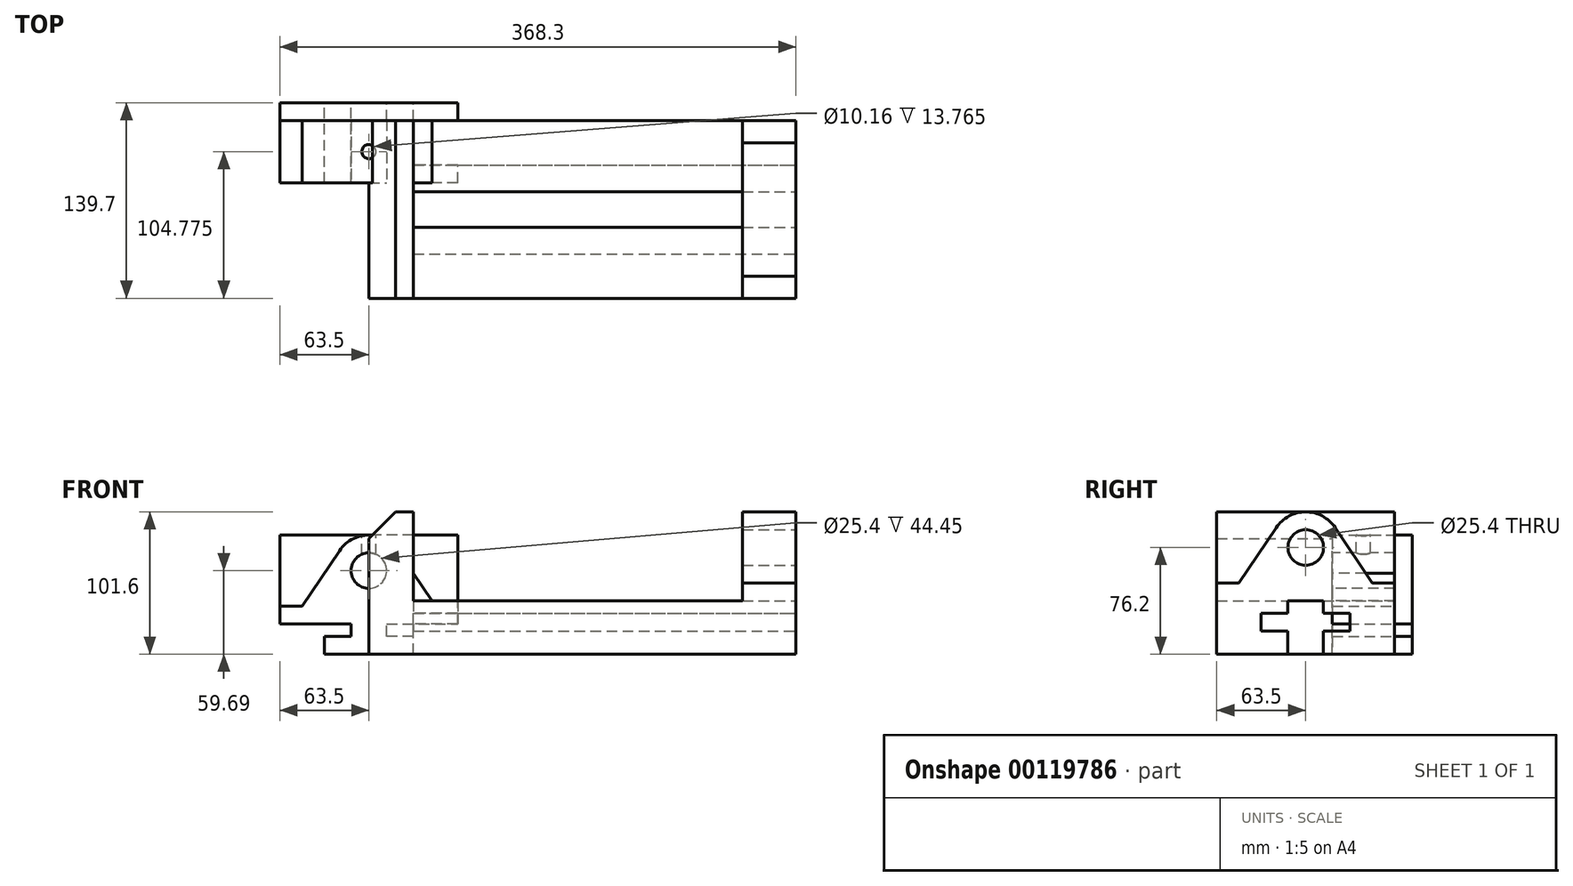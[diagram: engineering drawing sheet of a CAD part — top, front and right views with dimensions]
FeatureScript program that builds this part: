
annotation { "Feature Type Name" : "Feature", "Feature Type Description" : "" }
export const myFeature = defineFeature(function(context is Context, id is Id, definition is map)
    precondition{}
    {
        {
            var Q0;
            Q0=qCreatedBy(makeId("Front.planeOp"),FACE);
            var sketch = newSketch(context, id + "F0", { "sketchPlane" : qUnion([Q0])});
            skLineSegment(sketch, "E0", {"start": v(0, 0) * mm, "end": v(304.8, 0) * mm});
            skLineSegment(sketch, "E1", {"start": v(31.75, 38.1) * mm, "end": v(31.75, 101.6) * mm});
            skLineSegment(sketch, "E2", {"start": v(0, 101.6) * mm, "end": v(0, 0) * mm});
            skLineSegment(sketch, "E3", {"start": v(0, 101.6) * mm, "end": v(31.75, 101.6) * mm});
            skLineSegment(sketch, "E4", {"start": v(31.75, 38.1) * mm, "end": v(266.7, 38.1) * mm});
            skLineSegment(sketch, "E5", {"start": v(266.7, 38.1) * mm, "end": v(266.7, 101.6) * mm});
            skLineSegment(sketch, "E6", {"start": v(266.7, 101.6) * mm, "end": v(304.8, 101.6) * mm});
            skLineSegment(sketch, "E7", {"start": v(304.8, 101.6) * mm, "end": v(304.8, 0) * mm});
            skSolve(sketch);
        }
        {
            var Q0;
            Q0 = qSketchRegion(id + "F0", true);
            extrude(context, id + "F1", {"entities" : qUnion([Q0]), "depth" : 127 * mm});
        }
        {
            var Q0;
            Q0=makeQuery(id+"F1.opExtrude","SWEPT_EDGE",EDGE,{"disambiguationData":[OSD([sQuery(id+"F0.wireOp",EDGE,"E2"),sQuery(id+"F0.wireOp",EDGE,"E3")])]});
            chamfer(context, id + "F2", {"entities" : qUnion([Q0]), "chamferType" : ChamferType.TWO_OFFSETS, "width1" : 19.05 * mm, "oppositeDirection" : false, "width2" : 19.05 * mm, "tangentPropagation" : true});
        }
        {
            var Q0;
            Q0=makeQuery(id+"F1.opExtrude","SWEPT_FACE",FACE,{"disambiguationData":[OSD([sQuery(id+"F0.wireOp",EDGE,"E7")])]});
            var sketch = newSketch(context, id + "F3", { "sketchPlane" : qUnion([Q0])});
            skLineSegment(sketch, "E8", {"start": v(-127, 50.8) * mm, "end": v(-111.13, 50.8) * mm});
            skLineSegment(sketch, "E9", {"start": v(-111.13, 50.8) * mm, "end": v(-84.6, 90.35) * mm});
            skLineSegment(sketch, "E10", {"start": v(0, 50.8) * mm, "end": v(-15.87, 50.8) * mm});
            skLineSegment(sketch, "E11", {"start": v(-15.87, 50.8) * mm, "end": v(-42.4, 90.35) * mm});
            skArc(sketch, "E12", {"start": v(-42.4, 90.35) * mm, "mid": v(-63.5, 101.6) * mm, "end": v(-84.6, 90.35) * mm});
            skSolve(sketch);
        }
        {
            var Q0;
            Q0 = qSketchRegion(id + "F3", true);
            var Q1;
            {var subQ7=sQuery(id+"F3.wireOp",EDGE,"E8");Q1=makeQuery(id+"F3.imprint","IMPRINT",FACE,{"disambiguationData":[TD([[makeQuery(id+"F3.imprint","IMPRINT",EDGE,{"derivedFrom":subQ7}),1.0]])]});}
            var Q2;
            {var subQ7=sQuery(id+"F3.wireOp",EDGE,"E10");Q2=makeQuery(id+"F3.imprint","IMPRINT",FACE,{"disambiguationData":[TD([[makeQuery(id+"F3.imprint","IMPRINT",EDGE,{"derivedFrom":subQ7}),-1.0]])]});}
            extrude(context, id + "F4", {"entities" : qUnion([Q0, Q1, Q2]), "operationType" : NewBodyOperationType.REMOVE, "oppositeDirection" : true, "depth" : 50.8 * mm});
        }
        {
            var Q0;
            {var subQ6=sQuery(id+"F3.wireOp",EDGE,"E8");Q0=makeQuery(id+"F3.imprint","IMPRINT",FACE,{"disambiguationData":[TD([[makeQuery(id+"F3.imprint","IMPRINT",EDGE,{"derivedFrom":subQ6}),-1.0]])]});}
            var sketch = newSketch(context, id + "F5", { "sketchPlane" : qUnion([Q0])});
            skCircle(sketch, "E13", {"center": v(-63.5, 76.2) * mm, "radius": 12.7 * mm});
            skSolve(sketch);
        }
        {
            var Q0;
            Q0 = qSketchRegion(id + "F5", true);
            extrude(context, id + "F6", {"entities" : qUnion([Q0]), "operationType" : NewBodyOperationType.REMOVE, "oppositeDirection" : true, "depth" : 50.8 * mm});
        }
        {
            var Q0;
            {var subQ6=sQuery(id+"F3.wireOp",EDGE,"E8");Q0=makeQuery(id+"F3.imprint","IMPRINT",FACE,{"disambiguationData":[TD([[makeQuery(id+"F3.imprint","IMPRINT",EDGE,{"derivedFrom":subQ6}),-1.0]])]});}
            var sketch = newSketch(context, id + "F7", { "sketchPlane" : qUnion([Q0])});
            skLineSegment(sketch, "E14", {"start": v(-76.2, 0) * mm, "end": v(-76.2, 16.5) * mm});
            skLineSegment(sketch, "E15", {"start": v(-76.2, 16.5) * mm, "end": v(-95.25, 16.5) * mm});
            skLineSegment(sketch, "E16", {"start": v(-95.25, 16.5) * mm, "end": v(-95.25, 29.2) * mm});
            skLineSegment(sketch, "E17", {"start": v(-95.25, 29.2) * mm, "end": v(-76.2, 29.2) * mm});
            skLineSegment(sketch, "E18", {"start": v(-76.2, 29.2) * mm, "end": v(-76.2, 38.1) * mm});
            skLineSegment(sketch, "E19", {"start": v(-76.2, 38.1) * mm, "end": v(-50.8, 38.1) * mm});
            skLineSegment(sketch, "E20", {"start": v(-50.8, 38.1) * mm, "end": v(-50.8, 29.2) * mm});
            skLineSegment(sketch, "E21", {"start": v(-50.8, 29.2) * mm, "end": v(-31.75, 29.2) * mm});
            skLineSegment(sketch, "E22", {"start": v(-31.75, 29.2) * mm, "end": v(-31.75, 16.5) * mm});
            skLineSegment(sketch, "E23", {"start": v(-31.75, 16.5) * mm, "end": v(-50.8, 16.5) * mm});
            skLineSegment(sketch, "E24", {"start": v(-50.8, 16.5) * mm, "end": v(-50.8, 0) * mm});
            skLineSegment(sketch, "E25", {"start": v(-50.8, 0) * mm, "end": v(-76.2, 0) * mm});
            skSolve(sketch);
        }
        {
            var Q0;
            Q0 = qSketchRegion(id + "F7", true);
            var Q1;
            Q1=makeQuery(id+"F1.opExtrude","SWEPT_FACE",FACE,{"disambiguationData":[OSD([sQuery(id+"F0.wireOp",EDGE,"E1")])]});
            extrude(context, id + "F8", {"entities" : qUnion([Q0]), "operationType" : NewBodyOperationType.REMOVE, "endBound" : BoundingType.UP_TO_SURFACE, "oppositeDirection" : true, "endBoundEntityFace" : qUnion([Q1]), "depth" : 25.4 * mm});
        }
        {
            var Q0;
            Q0=qCreatedBy(makeId("Front.planeOp"),FACE);
            var sketch = newSketch(context, id + "F9", { "sketchPlane" : qUnion([Q0])});
            skLineSegment(sketch, "E26", {"start": v(0, 129.38) * mm, "end": v(0, -77.33) * mm, "construction": true});
            skLineSegment(sketch, "E27", {"start": v(-31.75, 0) * mm, "end": v(31.75, 0) * mm});
            skLineSegment(sketch, "E28", {"start": v(31.75, 0) * mm, "end": v(31.75, 12.7) * mm});
            skLineSegment(sketch, "E29", {"start": v(31.75, 12.7) * mm, "end": v(12.7, 12.7) * mm});
            skLineSegment(sketch, "E30", {"start": v(12.7, 12.7) * mm, "end": v(12.7, 21.6) * mm});
            skLineSegment(sketch, "E31", {"start": v(12.7, 21.59) * mm, "end": v(63.5, 21.59) * mm});
            skLineSegment(sketch, "E32", {"start": v(63.5, 21.59) * mm, "end": v(63.5, 34.3) * mm});
            skLineSegment(sketch, "E33", {"start": v(63.5, 34.3) * mm, "end": v(47.63, 34.3) * mm});
            skLineSegment(sketch, "E34", {"start": v(47.63, 34.29) * mm, "end": v(21.1, 73.84) * mm});
            skLineSegment(sketch, "E35", {"start": v(-31.75, 0) * mm, "end": v(-31.75, 12.7) * mm});
            skLineSegment(sketch, "E36", {"start": v(-31.75, 12.7) * mm, "end": v(-12.7, 12.7) * mm});
            skLineSegment(sketch, "E37", {"start": v(-12.7, 12.7) * mm, "end": v(-12.7, 21.59) * mm});
            skLineSegment(sketch, "E38", {"start": v(-12.7, 21.59) * mm, "end": v(-63.5, 21.59) * mm});
            skLineSegment(sketch, "E39", {"start": v(-63.5, 21.6) * mm, "end": v(-63.5, 34.3) * mm});
            skLineSegment(sketch, "E40", {"start": v(-63.5, 34.3) * mm, "end": v(-47.62, 34.3) * mm});
            skLineSegment(sketch, "E41", {"start": v(-47.62, 34.3) * mm, "end": v(-21.1, 73.84) * mm});
            skArc(sketch, "E42", {"start": v(21.1, 73.84) * mm, "mid": v(0, 85.1) * mm, "end": v(-21.1, 73.84) * mm});
            skSolve(sketch);
        }
        {
            var Q0;
            Q0 = qSketchRegion(id + "F9", true);
            extrude(context, id + "F10", {"entities" : qUnion([Q0]), "depth" : 44.45 * mm});
        }
        {
            var Q0;
            Q0=makeQuery(id+"F10.opExtrude","CAP_FACE",FACE,{"disambiguationData":[OSD([sQuery(id+"F9.wireOp",EDGE,"E27"),sQuery(id+"F9.wireOp",EDGE,"E28"),sQuery(id+"F9.wireOp",EDGE,"E29"),sQuery(id+"F9.wireOp",EDGE,"E30"),sQuery(id+"F9.wireOp",EDGE,"E31"),sQuery(id+"F9.wireOp",EDGE,"E32"),sQuery(id+"F9.wireOp",EDGE,"E33"),sQuery(id+"F9.wireOp",EDGE,"E34"),sQuery(id+"F9.wireOp",EDGE,"E35"),sQuery(id+"F9.wireOp",EDGE,"E36"),sQuery(id+"F9.wireOp",EDGE,"E37"),sQuery(id+"F9.wireOp",EDGE,"E38"),sQuery(id+"F9.wireOp",EDGE,"E39"),sQuery(id+"F9.wireOp",EDGE,"E40"),sQuery(id+"F9.wireOp",EDGE,"E41"),sQuery(id+"F9.wireOp",EDGE,"E42")])],"isStart":false});
            var sketch = newSketch(context, id + "F11", { "sketchPlane" : qUnion([Q0])});
            skCircle(sketch, "E43", {"center": v(0, 59.7) * mm, "radius": 12.7 * mm});
            skSolve(sketch);
        }
        {
            var Q0;
            Q0=makeQuery(id+"F11.imprint","IMPRINT",FACE,{"disambiguationData":[TD([[makeQuery(id+"F11.imprint","IMPRINT",EDGE,{"derivedFrom":sQuery(id+"F11.wireOp",EDGE,"E43")}),1.0]])]});
            extrude(context, id + "F12", {"entities" : qUnion([Q0]), "operationType" : NewBodyOperationType.REMOVE, "oppositeDirection" : true, "depth" : 44.45 * mm});
        }
        {
            var Q0;
            Q0=makeQuery(id+"F10.opExtrude","CAP_FACE",FACE,{"disambiguationData":[OSD([sQuery(id+"F9.wireOp",EDGE,"E27"),sQuery(id+"F9.wireOp",EDGE,"E28"),sQuery(id+"F9.wireOp",EDGE,"E29"),sQuery(id+"F9.wireOp",EDGE,"E30"),sQuery(id+"F9.wireOp",EDGE,"E31"),sQuery(id+"F9.wireOp",EDGE,"E32"),sQuery(id+"F9.wireOp",EDGE,"E33"),sQuery(id+"F9.wireOp",EDGE,"E34"),sQuery(id+"F9.wireOp",EDGE,"E35"),sQuery(id+"F9.wireOp",EDGE,"E36"),sQuery(id+"F9.wireOp",EDGE,"E37"),sQuery(id+"F9.wireOp",EDGE,"E38"),sQuery(id+"F9.wireOp",EDGE,"E39"),sQuery(id+"F9.wireOp",EDGE,"E40"),sQuery(id+"F9.wireOp",EDGE,"E41"),sQuery(id+"F9.wireOp",EDGE,"E42")])],"isStart":true});
            var sketch = newSketch(context, id + "F13", { "sketchPlane" : qUnion([Q0])});
            skLineSegment(sketch, "E44.bottom", {"start": v(-63.5, 0) * mm, "end": v(63.5, 0) * mm});
            skLineSegment(sketch, "E44.top", {"start": v(-63.5, 85.1) * mm, "end": v(63.5, 85.1) * mm});
            skLineSegment(sketch, "E44.left", {"start": v(-63.5, 0) * mm, "end": v(-63.5, 85.1) * mm});
            skLineSegment(sketch, "E44.right", {"start": v(63.5, 0) * mm, "end": v(63.5, 85.1) * mm});
            skSolve(sketch);
        }
        {
            var Q0;
            Q0 = qSketchRegion(id + "F13", true);
            extrude(context, id + "F14", {"entities" : qUnion([Q0]), "operationType" : NewBodyOperationType.ADD, "depth" : 12.7 * mm});
        }
        {
            var Q0;
            Q0=makeQuery(id+"F14.opExtrude","CAP_FACE",FACE,{"disambiguationData":[OSD([sQuery(id+"F13.wireOp",EDGE,"E44.bottom"),sQuery(id+"F13.wireOp",EDGE,"E44.top"),sQuery(id+"F13.wireOp",EDGE,"E44.left"),sQuery(id+"F13.wireOp",EDGE,"E44.right")])],"isStart":false});
            var sketch = newSketch(context, id + "F15", { "sketchPlane" : qUnion([Q0])});
            skLineSegment(sketch, "E45", {"start": v(-63.5, 0) * mm, "end": v(-31.75, 0) * mm});
            skLineSegment(sketch, "E46", {"start": v(-31.75, 0) * mm, "end": v(-31.75, 12.7) * mm});
            skLineSegment(sketch, "E47", {"start": v(-31.75, 12.7) * mm, "end": v(-12.7, 12.7) * mm});
            skLineSegment(sketch, "E48", {"start": v(-12.7, 12.7) * mm, "end": v(-12.7, 21.6) * mm});
            skLineSegment(sketch, "E49", {"start": v(-12.7, 21.6) * mm, "end": v(-63.5, 21.59) * mm});
            skLineSegment(sketch, "E50", {"start": v(-63.5, 21.6) * mm, "end": v(-63.5, 0) * mm});
            skLineSegment(sketch, "E51", {"start": v(12.7, 21.59) * mm, "end": v(63.5, 21.59) * mm});
            skLineSegment(sketch, "E52", {"start": v(63.5, 21.59) * mm, "end": v(63.5, 0) * mm});
            skLineSegment(sketch, "E53", {"start": v(63.5, 0) * mm, "end": v(31.75, 0) * mm});
            skLineSegment(sketch, "E54", {"start": v(31.75, 0) * mm, "end": v(31.75, 12.7) * mm});
            skLineSegment(sketch, "E55", {"start": v(31.75, 12.7) * mm, "end": v(12.7, 12.7) * mm});
            skLineSegment(sketch, "E56", {"start": v(12.7, 12.7) * mm, "end": v(12.7, 21.59) * mm});
            skSolve(sketch);
        }
        {
            var Q0;
            Q0 = qSketchRegion(id + "F15", true);
            extrude(context, id + "F16", {"entities" : qUnion([Q0]), "operationType" : NewBodyOperationType.REMOVE, "oppositeDirection" : true, "depth" : 12.7 * mm});
        }
        {
            var Q0;
            Q0=makeQuery(id+"F14.opExtrude","SWEPT_FACE",FACE,{"disambiguationData":[OSD([sQuery(id+"F13.wireOp",EDGE,"E44.top")])]});
            cPlane(context, id + "F17", {"entities" : qUnion([Q0]), "cplaneType" : CPlaneType.OFFSET, "offset" : 0 * mm, "width" : 152.4 * mm, "height" : 152.4 * mm});
        }
        {
            var Q0;
            Q0=qCreatedBy(id+"F17.planeOp",FACE);
            var sketch = newSketch(context, id + "F18", { "sketchPlane" : qUnion([Q0])});
            skLineSegment(sketch, "E57", {"start": v(0, -59.16) * mm, "end": v(0, 43.8) * mm, "construction": true});
            skCircle(sketch, "E58", {"center": v(0, -22.23) * mm, "radius": 5.08 * mm});
            skSolve(sketch);
        }
        {
            var Q0;
            Q0 = qSketchRegion(id + "F18", true);
            extrude(context, id + "F19", {"entities" : qUnion([Q0]), "operationType" : NewBodyOperationType.REMOVE, "oppositeDirection" : true, "depth" : 25.4 * mm});
        }
    });
